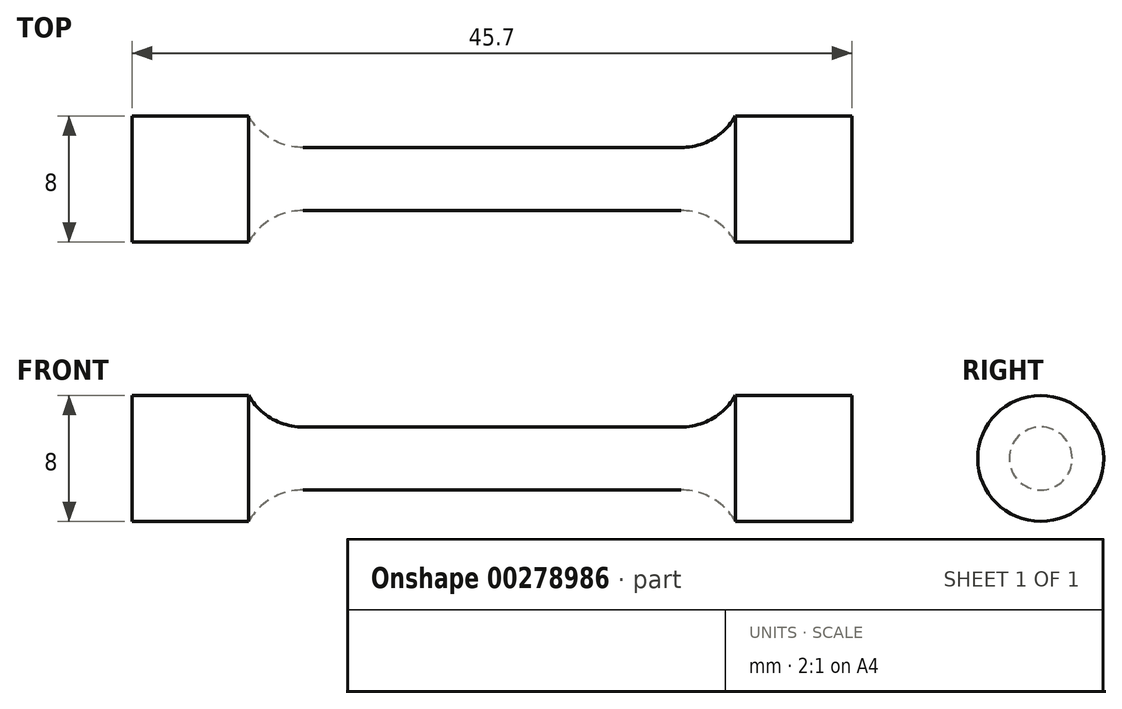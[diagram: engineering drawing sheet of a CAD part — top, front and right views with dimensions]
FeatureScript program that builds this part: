
annotation { "Feature Type Name" : "Feature", "Feature Type Description" : "" }
export const myFeature = defineFeature(function(context is Context, id is Id, definition is map)
    precondition{}
    {
        {
            var Q0;
            Q0=qCreatedBy(makeId("Front.planeOp"),FACE);
            var sketch = newSketch(context, id + "F0", { "sketchPlane" : qUnion([Q0])});
            skLineSegment(sketch, "E0", {"start": v(0, 2) * mm, "end": v(12, 2) * mm});
            skArc(sketch, "E1", {"start": v(12, 2) * mm, "mid": v(14, 2.54) * mm, "end": v(15.46, 4) * mm});
            skLineSegment(sketch, "E2", {"start": v(15.46, 4) * mm, "end": v(22.85, 4) * mm});
            skLineSegment(sketch, "E3", {"start": v(22.85, 4) * mm, "end": v(22.85, 0) * mm});
            skLineSegment(sketch, "E4.MirrorCS", {"start": v(0, 2) * mm, "end": v(-12, 2) * mm});
            skLineSegment(sketch, "E5.MirrorCS", {"start": v(-22.85, 4) * mm, "end": v(-22.85, 0) * mm});
            skLineSegment(sketch, "E6.MirrorCS", {"start": v(-15.46, 4) * mm, "end": v(-22.85, 4) * mm});
            skArc(sketch, "E7.MirrorCS", {"start": v(-12, 2) * mm, "mid": v(-14, 2.54) * mm, "end": v(-15.46, 4) * mm});
            skLineSegment(sketch, "E8", {"start": v(-22.85, 0) * mm, "end": v(22.85, 0) * mm});
            skSolve(sketch);
        }
        {
            var Q0;
            Q0 = qSketchRegion(id + "F0", true);
            var Q1;
            Q1=sQuery(id+"F0.wireOp",EDGE,"E8");
            revolve(context, id + "F1", {"entities" : qUnion([Q0]), "axis" : qUnion([Q1]), "revolveType" : RevolveType.FULL});
        }
    });
